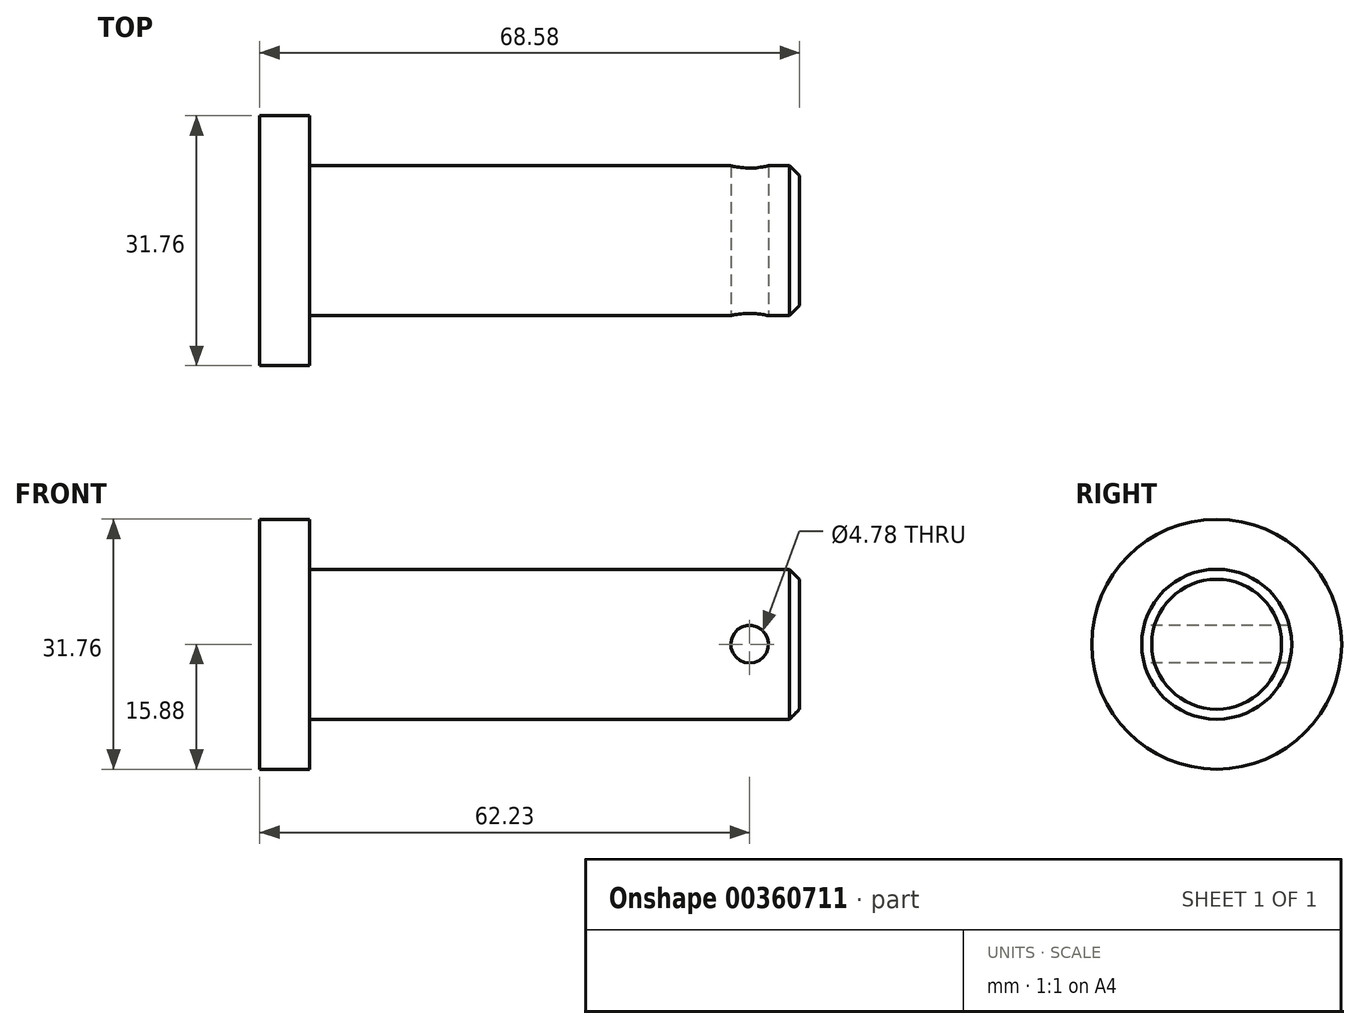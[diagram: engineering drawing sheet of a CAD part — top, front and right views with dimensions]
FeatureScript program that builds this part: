
annotation { "Feature Type Name" : "Feature", "Feature Type Description" : "" }
export const myFeature = defineFeature(function(context is Context, id is Id, definition is map)
    precondition{}
    {
        {
            var Q0;
            Q0=qCreatedBy(makeId("Right.planeOp"),FACE);
            var sketch = newSketch(context, id + "F0", { "sketchPlane" : qUnion([Q0])});
            skCircle(sketch, "E0", {"center": v(0, 0) * mm, "radius": 15.87 * mm});
            skSolve(sketch);
        }
        {
            var Q0;
            Q0=makeQuery(id+"F0.imprint","IMPRINT",FACE,{"disambiguationData":[TD([[makeQuery(id+"F0.imprint","IMPRINT",EDGE,{"derivedFrom":sQuery(id+"F0.wireOp",EDGE,"E0")}),1.0]])]});
            extrude(context, id + "F1", {"entities" : qUnion([Q0]), "depth" : 6.35 * mm});
        }
        {
            var Q0;
            Q0=makeQuery(id+"F1.opExtrude","CAP_FACE",FACE,{"disambiguationData":[OSD([sQuery(id+"F0.wireOp",EDGE,"E0")])],"isStart":false});
            var sketch = newSketch(context, id + "F2", { "sketchPlane" : qUnion([Q0])});
            skCircle(sketch, "E1", {"center": v(0, 0) * mm, "radius": 9.53 * mm});
            skSolve(sketch);
        }
        {
            var Q0;
            Q0=makeQuery(id+"F2.imprint","IMPRINT",FACE,{"disambiguationData":[TD([[makeQuery(id+"F2.imprint","IMPRINT",EDGE,{"derivedFrom":sQuery(id+"F2.wireOp",EDGE,"E1")}),1.0]])]});
            extrude(context, id + "F3", {"entities" : qUnion([Q0]), "operationType" : NewBodyOperationType.ADD, "depth" : 62.23 * mm});
        }
        {
            var Q0;
            Q0=qCreatedBy(makeId("Front.planeOp"),FACE);
            var sketch = newSketch(context, id + "F4", { "sketchPlane" : qUnion([Q0])});
            skLineSegment(sketch, "E2", {"start": v(0, 0) * mm, "end": v(68.58, 0) * mm, "construction": true});
            skLineSegment(sketch, "E3", {"start": v(68.58, 0) * mm, "end": v(62.23, 0) * mm, "construction": true});
            skCircle(sketch, "E4", {"center": v(62.23, 0) * mm, "radius": 2.39 * mm});
            skSolve(sketch);
        }
        {
            var Q0;
            Q0 = qSketchRegion(id + "F4", true);
            extrude(context, id + "F5", {"entities" : qUnion([Q0]), "operationType" : NewBodyOperationType.REMOVE, "endBound" : BoundingType.SYMMETRIC, "oppositeDirection" : true, "depth" : 127 * mm});
        }
        {
            var Q0;
            Q0=makeQuery(id+"F3.opExtrude","CAP_EDGE",EDGE,{"disambiguationData":[OSD([sQuery(id+"F2.wireOp",EDGE,"E1")])],"isStart":false});
            chamfer(context, id + "F6", {"entities" : qUnion([Q0]), "width" : 1.27 * mm, "tangentPropagation" : true});
        }
    });
